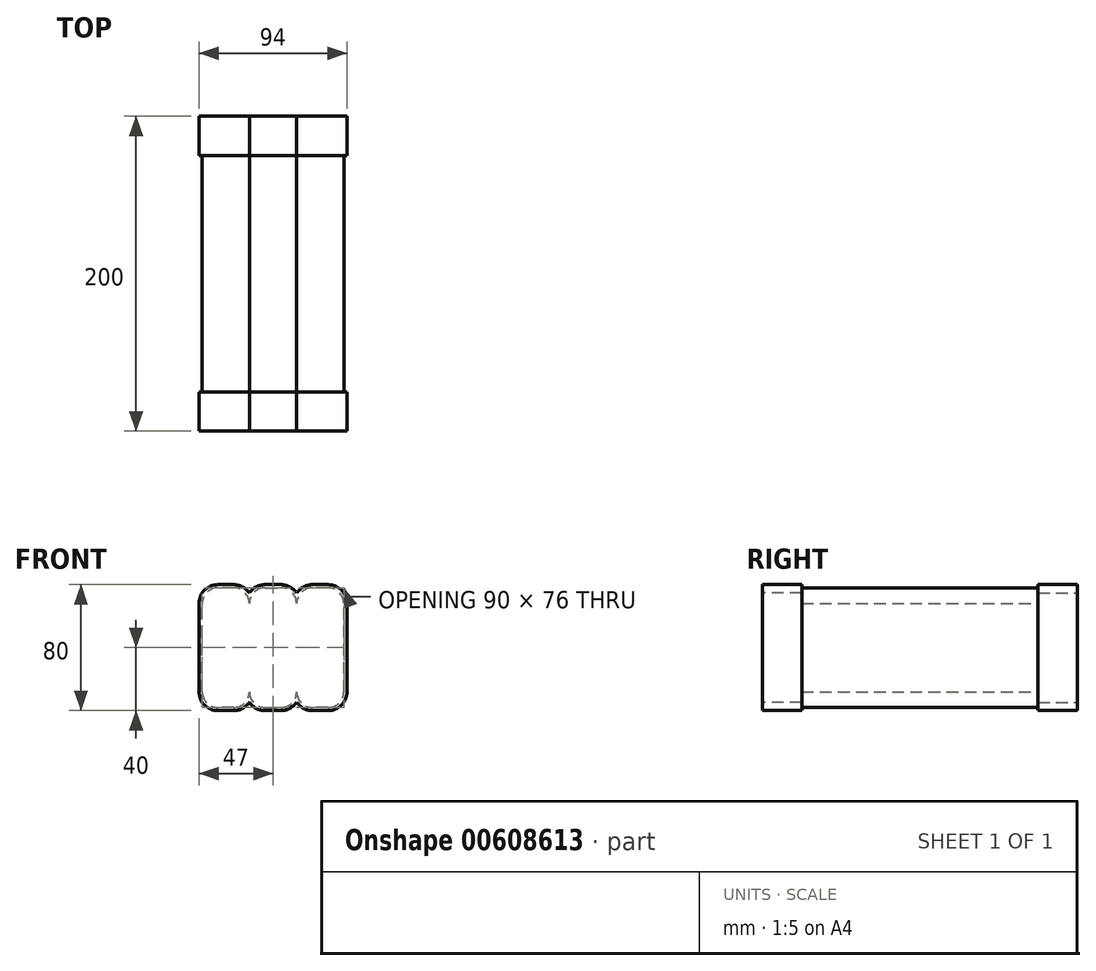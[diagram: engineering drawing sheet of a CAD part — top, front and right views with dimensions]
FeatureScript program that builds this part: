
annotation { "Feature Type Name" : "Feature", "Feature Type Description" : "" }
export const myFeature = defineFeature(function(context is Context, id is Id, definition is map)
    precondition{}
    {
        {
            var Q0;
            Q0=qCreatedBy(makeId("Right.planeOp"),FACE);
            var sketch = newSketch(context, id + "F0", { "sketchPlane" : qUnion([Q0])});
            skLineSegment(sketch, "E0.bottom", {"start": v(0, 0) * mm, "end": v(100, 0) * mm});
            skLineSegment(sketch, "E0.top", {"start": v(0, 76) * mm, "end": v(100, 76) * mm});
            skLineSegment(sketch, "E0.left", {"start": v(0, 0) * mm, "end": v(0, 76) * mm});
            skLineSegment(sketch, "E0.right", {"start": v(100, 0) * mm, "end": v(100, 76) * mm});
            skSolve(sketch);
        }
        {
            var Q0;
            Q0=makeQuery(id+"F0.imprint","IMPRINT",FACE,{"disambiguationData":[TD([[makeQuery(id+"F0.imprint","IMPRINT",EDGE,{"derivedFrom":sQuery(id+"F0.wireOp",EDGE,"E0.bottom")}),1.0]])]});
            extrude(context, id + "F1", {"entities" : qUnion([Q0]), "depth" : 30 * mm, "offsetDistance" : 25 * mm});
        }
        {
            var Q0;
            Q0=makeQuery(id+"F1.opExtrude","CAP_EDGE",EDGE,{"disambiguationData":[OSD([sQuery(id+"F0.wireOp",EDGE,"E0.top")])],"isStart":false});
            var Q1;
            Q1=makeQuery(id+"F1.opExtrude","CAP_EDGE",EDGE,{"disambiguationData":[OSD([sQuery(id+"F0.wireOp",EDGE,"E0.top")])],"isStart":true});
            var Q2;
            Q2=makeQuery(id+"F1.opExtrude","CAP_EDGE",EDGE,{"disambiguationData":[OSD([sQuery(id+"F0.wireOp",EDGE,"E0.bottom")])],"isStart":false});
            var Q3;
            Q3=makeQuery(id+"F1.opExtrude","CAP_EDGE",EDGE,{"disambiguationData":[OSD([sQuery(id+"F0.wireOp",EDGE,"E0.bottom")])],"isStart":true});
            fillet(context, id + "F2", {"entities" : qUnion([Q0, Q1, Q2, Q3]), "radius" : 10 * mm, "tangentPropagation" : true, "allowEdgeOverflow" : false});
        }
        {
            var Q0;
            Q0=makeQuery(id+"F1.opExtrude","SWEPT_BODY",BODY,{"disambiguationData":[OSD([sQuery(id+"F0.wireOp",EDGE,"E0.bottom"),sQuery(id+"F0.wireOp",EDGE,"E0.top"),sQuery(id+"F0.wireOp",EDGE,"E0.left"),sQuery(id+"F0.wireOp",EDGE,"E0.right")])]});
            var Q1;
            Q1=makeQuery(id+"F1.opExtrude","CAP_FACE",FACE,{"disambiguationData":[OSD([sQuery(id+"F0.wireOp",EDGE,"E0.bottom"),sQuery(id+"F0.wireOp",EDGE,"E0.top"),sQuery(id+"F0.wireOp",EDGE,"E0.left"),sQuery(id+"F0.wireOp",EDGE,"E0.right")])],"isStart":false});
            mirror(context, id + "F3", {"operationType" : NewBodyOperationType.ADD, "entities" : qUnion([Q0]), "mirrorPlane" : qUnion([Q1])});
        }
        {
            var Q0;
            Q0=makeQuery(id+"F1.opExtrude","SWEPT_BODY",BODY,{"disambiguationData":[OSD([sQuery(id+"F0.wireOp",EDGE,"E0.bottom"),sQuery(id+"F0.wireOp",EDGE,"E0.top"),sQuery(id+"F0.wireOp",EDGE,"E0.left"),sQuery(id+"F0.wireOp",EDGE,"E0.right")])]});
            var Q1;
            Q1=makeQuery(id+"F3.opPattern","COPY",FACE,{"derivedFrom":makeQuery(id+"F1.opExtrude","CAP_FACE",FACE,{"disambiguationData":[OSD([sQuery(id+"F0.wireOp",EDGE,"E0.bottom"),sQuery(id+"F0.wireOp",EDGE,"E0.top"),sQuery(id+"F0.wireOp",EDGE,"E0.left"),sQuery(id+"F0.wireOp",EDGE,"E0.right")])],"isStart":true}),"instanceName":"1"});
            mirror(context, id + "F4", {"operationType" : NewBodyOperationType.ADD, "entities" : qUnion([Q0]), "mirrorPlane" : qUnion([Q1])});
        }
        {
            var Q0;
            Q0=makeQuery(id+"F4.opPattern","COPY",FACE,{"derivedFrom":makeQuery(id+"F1.opExtrude","CAP_FACE",FACE,{"disambiguationData":[OSD([sQuery(id+"F0.wireOp",EDGE,"E0.bottom"),sQuery(id+"F0.wireOp",EDGE,"E0.top"),sQuery(id+"F0.wireOp",EDGE,"E0.left"),sQuery(id+"F0.wireOp",EDGE,"E0.right")])],"isStart":true}),"instanceName":"1"});
            var sketch = newSketch(context, id + "F5", { "sketchPlane" : qUnion([Q0])});
            skLineSegment(sketch, "E1.bottom", {"start": v(-5, 86) * mm, "end": v(110, 86) * mm});
            skLineSegment(sketch, "E1.top", {"start": v(-5, -10) * mm, "end": v(110, -10) * mm});
            skLineSegment(sketch, "E1.left", {"start": v(-5, 86) * mm, "end": v(-5, -10) * mm});
            skLineSegment(sketch, "E1.right", {"start": v(110, 86) * mm, "end": v(110, -10) * mm});
            skSolve(sketch);
        }
        {
            var Q0;
            Q0=makeQuery(id+"F5.imprint","IMPRINT",FACE,{"disambiguationData":[TD([[makeQuery(id+"F5.imprint","IMPRINT",EDGE,{"derivedFrom":sQuery(id+"F5.wireOp",EDGE,"E1.bottom")}),-1.0]])]});
            var Q1;
            {var subQ1=sQuery(id+"F0.wireOp",EDGE,"E0.left");Q1=makeQuery(id+"F5.imprint","IMPRINT",FACE,{"disambiguationData":[TD([[makeQuery(id+"F5.imprint","IMPRINT",EDGE,{"derivedFrom":makeQuery(id+"F4.opPattern","COPY",EDGE,{"derivedFrom":makeQuery(id+"F1.opExtrude","CAP_EDGE",EDGE,{"disambiguationData":[OSD([subQ1])],"isStart":true}),"instanceName":"1"})}),-1.0]])]});}
            extrude(context, id + "F6", {"entities" : qUnion([Q0, Q1]), "operationType" : NewBodyOperationType.REMOVE, "oppositeDirection" : true, "depth" : 30 * mm, "offsetDistance" : 25 * mm});
        }
        {
            var Q0;
            {var subQ0=makeQuery(id+"F1.opExtrude","SWEPT_FACE",FACE,{"disambiguationData":[OSD([sQuery(id+"F0.wireOp",EDGE,"E0.left")])]});var subQ1=makeQuery(id+"F3.boolean.opBoolean","MERGE",FACE,{"derivedFrom":[subQ0,makeQuery(id+"F3.opPattern","COPY",FACE,{"derivedFrom":subQ0,"instanceName":"1"})]});Q0=makeQuery(id+"F4.boolean.opBoolean","MERGE",FACE,{"derivedFrom":[subQ1,makeQuery(id+"F4.opPattern","COPY",FACE,{"derivedFrom":subQ1,"instanceName":"1"})]});}
            var sketch = newSketch(context, id + "F7", { "sketchPlane" : qUnion([Q0])});
            skLineSegment(sketch, "E2.0", {"start": v(70, -2) * mm, "end": v(80, -2) * mm});
            skArc(sketch, "E2.1", {"start": v(60, 3.37) * mm, "mid": v(64.33, -0.57) * mm, "end": v(70, -2) * mm});
            skArc(sketch, "E2.2", {"start": v(50, -2) * mm, "mid": v(55.67, -0.57) * mm, "end": v(60, 3.37) * mm});
            skLineSegment(sketch, "E2.3", {"start": v(40, -2) * mm, "end": v(50, -2) * mm});
            skArc(sketch, "E2.4", {"start": v(30, 3.37) * mm, "mid": v(34.33, -0.57) * mm, "end": v(40, -2) * mm});
            skArc(sketch, "E2.5", {"start": v(80, -2) * mm, "mid": v(88.49, 1.51) * mm, "end": v(92, 10) * mm});
            skArc(sketch, "E2.6", {"start": v(20, -2) * mm, "mid": v(25.67, -0.57) * mm, "end": v(30, 3.37) * mm});
            skLineSegment(sketch, "E2.7", {"start": v(10, -2) * mm, "end": v(20, -2) * mm});
            skArc(sketch, "E2.8", {"start": v(-2, 10) * mm, "mid": v(1.51, 1.51) * mm, "end": v(10, -2) * mm});
            skLineSegment(sketch, "E2.9", {"start": v(-2, 66) * mm, "end": v(-2, 10) * mm});
            skArc(sketch, "E2.10", {"start": v(70, 78) * mm, "mid": v(64.33, 76.57) * mm, "end": v(60, 72.63) * mm});
            skLineSegment(sketch, "E2.11", {"start": v(80, 78) * mm, "end": v(70, 78) * mm});
            skArc(sketch, "E2.12", {"start": v(92, 66) * mm, "mid": v(88.49, 74.49) * mm, "end": v(80, 78) * mm});
            skLineSegment(sketch, "E2.13", {"start": v(92, 10) * mm, "end": v(92, 66) * mm});
            skArc(sketch, "E2.14", {"start": v(60, 72.63) * mm, "mid": v(55.67, 76.57) * mm, "end": v(50, 78) * mm});
            skLineSegment(sketch, "E2.15", {"start": v(50, 78) * mm, "end": v(40, 78) * mm});
            skArc(sketch, "E2.16", {"start": v(40, 78) * mm, "mid": v(34.33, 76.57) * mm, "end": v(30, 72.63) * mm});
            skArc(sketch, "E2.17", {"start": v(30, 72.63) * mm, "mid": v(25.67, 76.57) * mm, "end": v(20, 78) * mm});
            skLineSegment(sketch, "E2.18", {"start": v(20, 78) * mm, "end": v(10, 78) * mm});
            skArc(sketch, "E2.19", {"start": v(10, 78) * mm, "mid": v(1.51, 74.49) * mm, "end": v(-2, 66) * mm});
            skSolve(sketch);
        }
        {
            var Q0;
            Q0=makeQuery(id+"F7.imprint","IMPRINT",FACE,{"disambiguationData":[TD([[makeQuery(id+"F7.imprint","IMPRINT",EDGE,{"derivedFrom":sQuery(id+"F7.wireOp",EDGE,"E2.0")}),1.0]])]});
            extrude(context, id + "F8", {"entities" : qUnion([Q0]), "operationType" : NewBodyOperationType.ADD, "oppositeDirection" : true, "depth" : 25 * mm, "offsetDistance" : 25 * mm});
        }
        {
            var Q0;
            Q0=makeQuery(id+"F1.opExtrude","SWEPT_BODY",BODY,{"disambiguationData":[OSD([sQuery(id+"F0.wireOp",EDGE,"E0.bottom"),sQuery(id+"F0.wireOp",EDGE,"E0.top"),sQuery(id+"F0.wireOp",EDGE,"E0.left"),sQuery(id+"F0.wireOp",EDGE,"E0.right")])]});
            var Q1;
            {var subQ0=makeQuery(id+"F1.opExtrude","SWEPT_FACE",FACE,{"disambiguationData":[OSD([sQuery(id+"F0.wireOp",EDGE,"E0.right")])]});var subQ1=makeQuery(id+"F3.boolean.opBoolean","MERGE",FACE,{"derivedFrom":[subQ0,makeQuery(id+"F3.opPattern","COPY",FACE,{"derivedFrom":subQ0,"instanceName":"1"})]});Q1=makeQuery(id+"F4.boolean.opBoolean","MERGE",FACE,{"derivedFrom":[subQ1,makeQuery(id+"F4.opPattern","COPY",FACE,{"derivedFrom":subQ1,"instanceName":"1"})]});}
            mirror(context, id + "F9", {"operationType" : NewBodyOperationType.ADD, "entities" : qUnion([Q0]), "mirrorPlane" : qUnion([Q1])});
        }
    });
